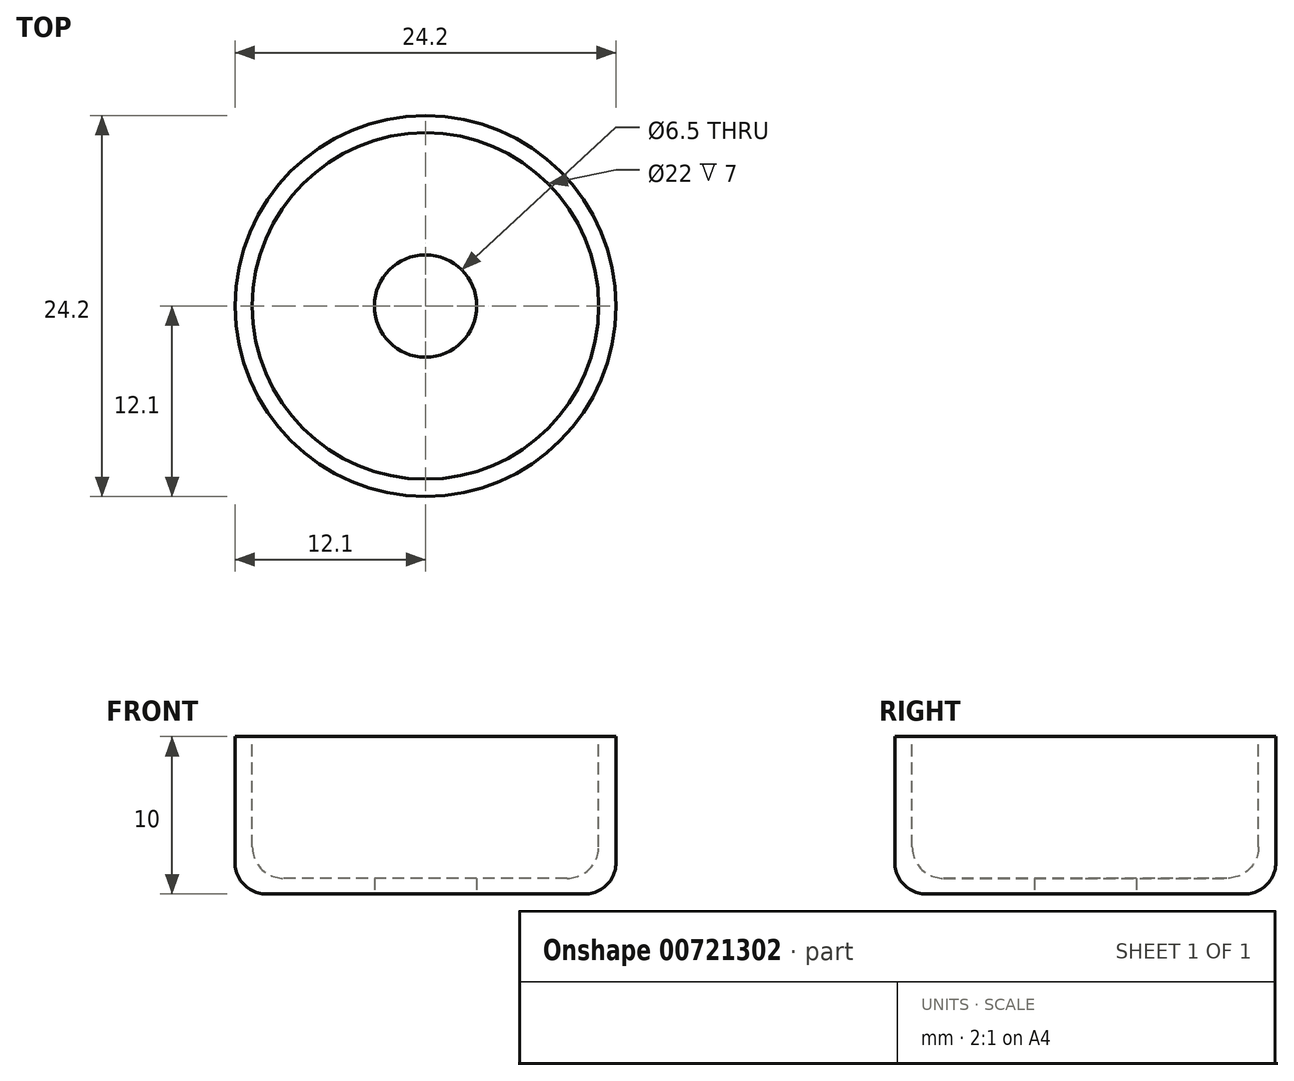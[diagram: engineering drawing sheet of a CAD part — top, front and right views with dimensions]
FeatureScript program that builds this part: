
annotation { "Feature Type Name" : "Feature", "Feature Type Description" : "" }
export const myFeature = defineFeature(function(context is Context, id is Id, definition is map)
    precondition{}
    {
        {
            var Q0;
            Q0=qCreatedBy(makeId("Top.planeOp"),FACE);
            var sketch = newSketch(context, id + "F0", { "sketchPlane" : qUnion([Q0])});
            skCircle(sketch, "E0", {"center": v(0, 0) * mm, "radius": 12.1 * mm});
            skCircle(sketch, "E1", {"center": v(0, 0) * mm, "radius": 3.25 * mm});
            skSolve(sketch);
        }
        {
            var Q0;
            Q0=makeQuery(id+"F0.imprint","IMPRINT",FACE,{"disambiguationData":[TD([[makeQuery(id+"F0.imprint","IMPRINT",EDGE,{"derivedFrom":sQuery(id+"F0.wireOp",EDGE,"E0")}),1.0]])]});
            extrude(context, id + "F1", {"entities" : qUnion([Q0]), "depth" : 10 * mm, "offsetDistance" : 25 * mm});
        }
        {
            var Q0;
            Q0=makeQuery(id+"F1.opExtrude","CAP_FACE",FACE,{"disambiguationData":[OSD([sQuery(id+"F0.wireOp",EDGE,"E0"),sQuery(id+"F0.wireOp",EDGE,"E1")])],"isStart":false});
            var sketch = newSketch(context, id + "F2", { "sketchPlane" : qUnion([Q0])});
            skCircle(sketch, "E2", {"center": v(0, 0) * mm, "radius": 11 * mm});
            skSolve(sketch);
        }
        {
            var Q0;
            Q0=makeQuery(id+"F2.imprint","IMPRINT",FACE,{"disambiguationData":[TD([[makeQuery(id+"F2.imprint","IMPRINT",EDGE,{"derivedFrom":sQuery(id+"F2.wireOp",EDGE,"E2")}),1.0]])]});
            extrude(context, id + "F3", {"entities" : qUnion([Q0]), "operationType" : NewBodyOperationType.REMOVE, "oppositeDirection" : true, "depth" : 9 * mm, "offsetDistance" : 25 * mm});
        }
        {
            var Q0;
            Q0=makeQuery(id+"F1.opExtrude","CAP_EDGE",EDGE,{"disambiguationData":[OSD([sQuery(id+"F0.wireOp",EDGE,"E0")])],"isStart":true});
            fillet(context, id + "F4", {"entities" : qUnion([Q0]), "radius" : 2 * mm, "tangentPropagation" : true, "allowEdgeOverflow" : false});
        }
        {
            var Q0;
            Q0=makeQuery(id+"F3.boolean.opBoolean","COPY",EDGE,{"derivedFrom":makeQuery(id+"F3.opExtrude","CAP_EDGE",EDGE,{"disambiguationData":[OSD([sQuery(id+"F2.wireOp",EDGE,"E2")])],"isStart":false})});
            fillet(context, id + "F5", {"entities" : qUnion([Q0]), "radius" : 2 * mm, "tangentPropagation" : true, "allowEdgeOverflow" : false});
        }
    });
